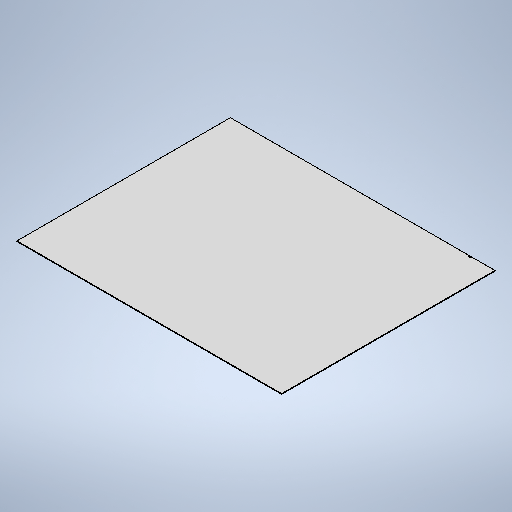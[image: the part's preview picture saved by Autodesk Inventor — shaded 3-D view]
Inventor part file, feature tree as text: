
AUTODESK INVENTOR PART (.ipt)
format: ipt  version: 2025.3 (Build 293356000, 356)  size: 295,936 bytes
history: native  units: mm
features: other x3, sketch x2, sheet_metal_op x1
ambient origin geometry x8: Origin, YZ Plane, XZ Plane, XY Plane, X Axis, Y Axis, Z Axis, Center Point
bodies: Solid1 (feature_tree)
feature tree (6):
  sheet_metal_op  "Face1"
  sketch  "Sketch1"  dims[d2=3.0mm]
  other  "Plate1"
  sketch  "Sketch5"  dims[d22=1240.0mm d23=1000.0mm d24=35.0mm d25=35.0mm d28=90.0mm d29=970.0mm d30=100.0mm d31=2.0mm d32=5.0mm d33=4.0mm d34=0.5mm d35=5.0mm d36=5.0mm d37=5.0mm d38=2.0mm d39=3.0mm d40=0.0mm]
  other  "Cut1"
  other  "Definition1"
